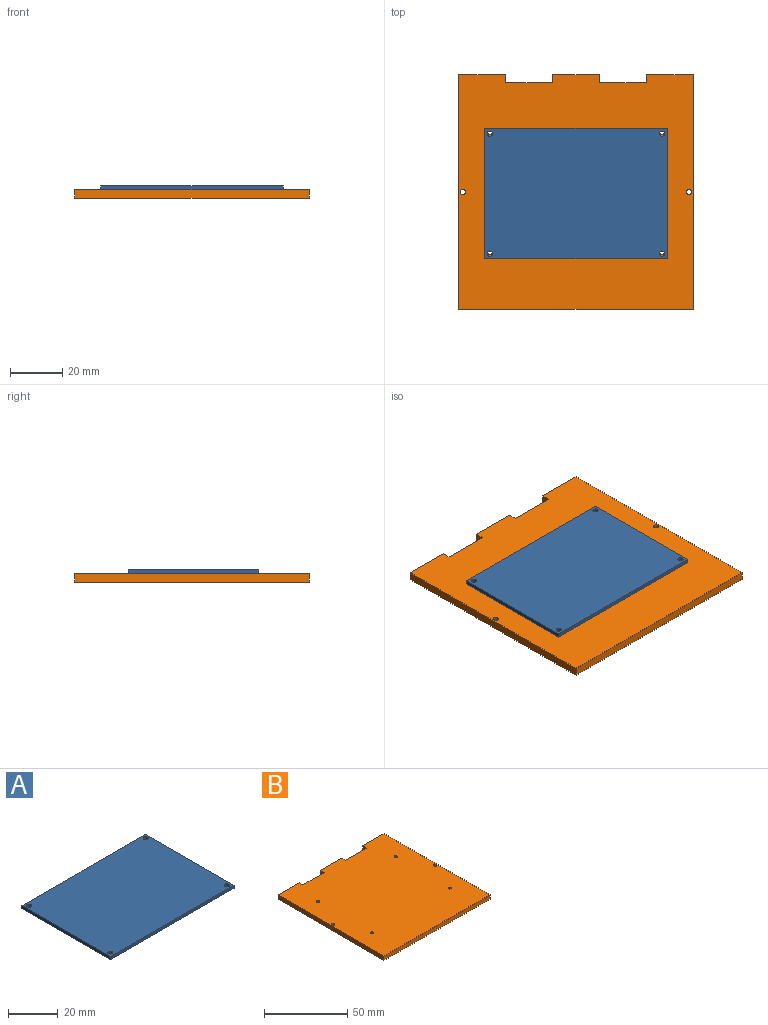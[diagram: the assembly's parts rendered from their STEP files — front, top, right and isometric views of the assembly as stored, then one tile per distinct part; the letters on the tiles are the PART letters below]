
ASSEMBLY  parts=2 mates=1
PART A: 10 faces, bbox 70x50x1.5 mm
  f0: plane 50x1.5mm, normal (1,0,0), area 75mm2, adj f1,f6,f8,f9
  f1: plane 70x1.5mm, normal (0,1,0), area 105mm2, adj f0,f2,f8,f9
  f2: plane 50x1.5mm, normal (-1,0,0), area 75mm2, adj f1,f6,f8,f9
  f3: cylinder r=1mm len=2mm, axis (0,0,-1), area 9.4mm2, adj f8,f9
  f4: cylinder r=1mm len=2mm, axis (0,0,-1), area 9.4mm2, adj f8,f9
  f5: cylinder r=1mm len=2mm, axis (0,0,-1), area 9.4mm2, adj f8,f9
  f6: plane 70x1.5mm, normal (0,-1,0), area 105mm2, adj f0,f2,f8,f9
  f7: cylinder r=1mm len=2mm, axis (0,0,-1), area 9.4mm2, adj f8,f9
  f8: plane 70x50mm, normal (0,0,1), area 3487.4mm2, adj f0,f1,f2,f3,f4,f5,f6,f7
  f9: plane 70x50mm, normal (0,0,-1), area 3487.4mm2, adj f0,f1,f2,f3,f4,f5,f6,f7
PART B: 20 faces, bbox 90x90x3.2 mm
  f0: plane 18x3.18mm, normal (0,1,0), area 57.1mm2, adj f2,f12,f13,f18
  f1: plane 18x3.18mm, normal (0,1,0), area 57.1mm2, adj f12,f13,f16,f19
  f2: plane 90x3.18mm, normal (1,0,0), area 285.8mm2, adj f0,f10,f12,f13
  f3: plane 18x3.18mm, normal (0,1,0), area 57.1mm2, adj f4,f12,f13,f15
  f4: plane 90x3.18mm, normal (-1,0,0), area 285.8mm2, adj f3,f10,f12,f13
  f5: cylinder r=1mm len=3.18mm, axis (0,0,-1), area 19.9mm2, adj f12,f13
  f6: cylinder r=1mm len=3.18mm, axis (0,0,-1), area 19.9mm2, adj f12,f13
  f7: cylinder r=1mm len=3.18mm, axis (0,0,-1), area 19.9mm2, adj f12,f13
  f8: cylinder r=1mm len=3.18mm, axis (0,0,-1), area 19.9mm2, adj f12,f13
  f9: cylinder r=1mm len=3.18mm, axis (0,0,-1), area 19.9mm2, adj f12,f13
  f10: plane 90x3.18mm, normal (0,-1,0), area 285.8mm2, adj f2,f4,f12,f13
  f11: cylinder r=1mm len=3.18mm, axis (0,0,-1), area 19.9mm2, adj f12,f13
  f12: plane 90x90mm, normal (0,0,1), area 7966.9mm2, adj f0,f1,f2,f3,f4,f5,f6,f7
  f13: plane 90x90mm, normal (0,0,-1), area 7966.9mm2, adj f0,f1,f2,f3,f4,f5,f6,f7
  f14: plane 18x3.18mm, normal (0,1,0), area 57.1mm2, adj f12,f13,f15,f16
  f15: plane 3.18x3.18mm, normal (1,0,0), area 10.1mm2, adj f3,f12,f13,f14
  f16: plane 3.18x3.18mm, normal (-1,0,0), area 10.1mm2, adj f1,f12,f13,f14
  f17: plane 18x3.18mm, normal (0,1,0), area 57.1mm2, adj f12,f13,f18,f19
  f18: plane 3.18x3.18mm, normal (-1,0,0), area 10.1mm2, adj f0,f12,f13,f17
  f19: plane 3.18x3.18mm, normal (1,0,0), area 10.1mm2, adj f1,f12,f13,f17
PLACE A t=(-7.63,-8.16,-3.11)mm
PLACE B t=(-7.63,-7.54,-6.28)mm
MATE fastened A.f9 <-> B.f12  axis (0,0,-1) through (-7.63,-8.16,-3.11)mm
